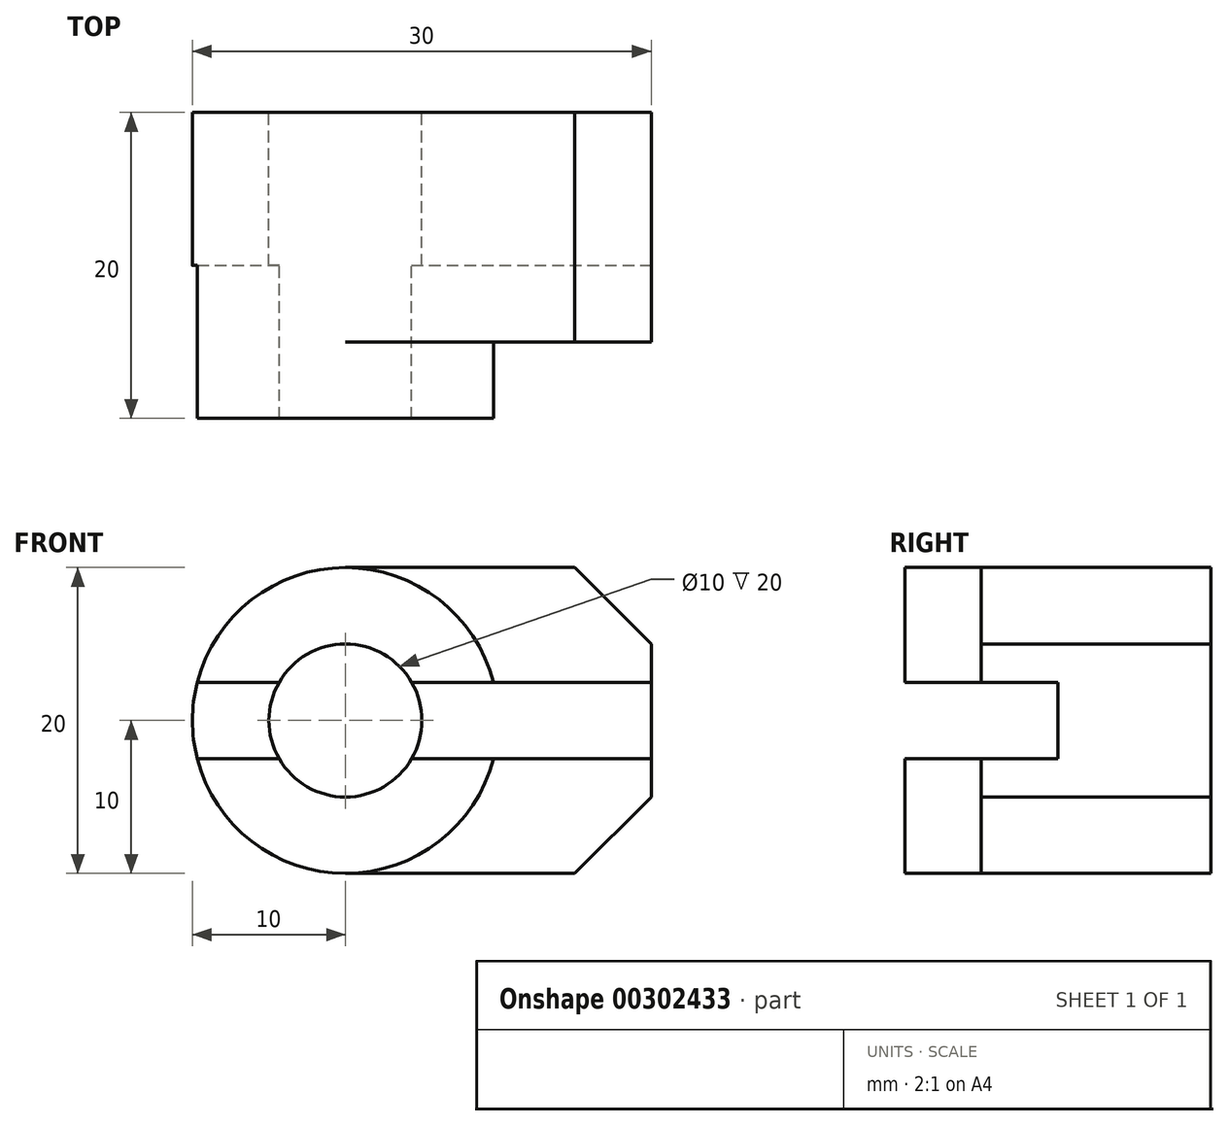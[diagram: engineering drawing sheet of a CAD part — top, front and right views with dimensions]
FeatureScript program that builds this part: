
annotation { "Feature Type Name" : "Feature", "Feature Type Description" : "" }
export const myFeature = defineFeature(function(context is Context, id is Id, definition is map)
    precondition{}
    {
        {
            var Q0;
            Q0=qCreatedBy(makeId("Front.planeOp"),FACE);
            var sketch = newSketch(context, id + "F0", { "sketchPlane" : qUnion([Q0])});
            skCircle(sketch, "E0", {"center": v(0, 0) * mm, "radius": 10 * mm});
            skLineSegment(sketch, "E1", {"start": v(0, 10) * mm, "end": v(15, 10) * mm});
            skLineSegment(sketch, "E2", {"start": v(0, -10) * mm, "end": v(15, -10) * mm});
            skLineSegment(sketch, "E3", {"start": v(15, 10) * mm, "end": v(20, 5) * mm});
            skLineSegment(sketch, "E4", {"start": v(20, 5) * mm, "end": v(20, -5) * mm});
            skLineSegment(sketch, "E5", {"start": v(20, -5) * mm, "end": v(15, -10) * mm});
            skCircle(sketch, "E6", {"center": v(0, 0) * mm, "radius": 5 * mm});
            skSolve(sketch);
        }
        {
            var Q0;
            {var subQ1=sQuery(id+"F0.wireOp",EDGE,"E1");Q0=makeQuery(id+"F0.imprint","IMPRINT",FACE,{"disambiguationData":[TD([[makeQuery(id+"F0.imprint","IMPRINT",EDGE,{"derivedFrom":subQ1}),-1.0]])]});}
            extrude(context, id + "F1", {"entities" : qUnion([Q0]), "depth" : 15 * mm});
        }
        {
            var Q0;
            Q0=makeQuery(id+"F0.imprint","IMPRINT",FACE,{"disambiguationData":[TD([[makeQuery(id+"F0.imprint","IMPRINT",EDGE,{"derivedFrom":sQuery(id+"F0.wireOp",EDGE,"E6")}),-1.0]])]});
            extrude(context, id + "F2", {"entities" : qUnion([Q0]), "operationType" : NewBodyOperationType.ADD, "depth" : 20 * mm});
        }
        {
            var Q0;
            Q0=makeQuery(id+"F1.opExtrude","SWEPT_FACE",FACE,{"disambiguationData":[OSD([sQuery(id+"F0.wireOp",EDGE,"E4")])]});
            var sketch = newSketch(context, id + "F3", { "sketchPlane" : qUnion([Q0])});
            skLineSegment(sketch, "E7", {"start": v(-20, 2.5) * mm, "end": v(-10, 2.5) * mm});
            skLineSegment(sketch, "E8", {"start": v(-10, 2.5) * mm, "end": v(-10, -2.5) * mm});
            skLineSegment(sketch, "E9", {"start": v(-10, -2.5) * mm, "end": v(-20, -2.5) * mm});
            skLineSegment(sketch, "E10", {"start": v(-20, -2.5) * mm, "end": v(-20, 2.5) * mm});
            skLineSegment(sketch, "E11", {"start": v(-15, 2.5) * mm, "end": v(-15, 5) * mm});
            skLineSegment(sketch, "E12", {"start": v(-15, 5) * mm, "end": v(0, 5) * mm});
            skLineSegment(sketch, "E13", {"start": v(0, 5) * mm, "end": v(0, -5) * mm});
            skLineSegment(sketch, "E14", {"start": v(0, -5) * mm, "end": v(-15, -5) * mm});
            skLineSegment(sketch, "E15", {"start": v(-15, -5) * mm, "end": v(-15, -2.5) * mm});
            skSolve(sketch);
        }
        {
            var Q0;
            {var subQ0=sQuery(id+"F3.wireOp",EDGE,"E8");Q0=makeQuery(id+"F3.imprint","IMPRINT",FACE,{"disambiguationData":[TD([[makeQuery(id+"F3.imprint","IMPRINT",EDGE,{"derivedFrom":subQ0}),-1.0]])]});}
            var Q1;
            {var subQ0=sQuery(id+"F3.wireOp",EDGE,"E10");Q1=makeQuery(id+"F3.imprint","IMPRINT",FACE,{"disambiguationData":[TD([[makeQuery(id+"F3.imprint","IMPRINT",EDGE,{"derivedFrom":subQ0}),-1.0]])]});}
            extrude(context, id + "F4", {"entities" : qUnion([Q0, Q1]), "operationType" : NewBodyOperationType.REMOVE, "endBound" : BoundingType.THROUGH_ALL, "oppositeDirection" : true, "depth" : 25 * mm});
        }
    });
